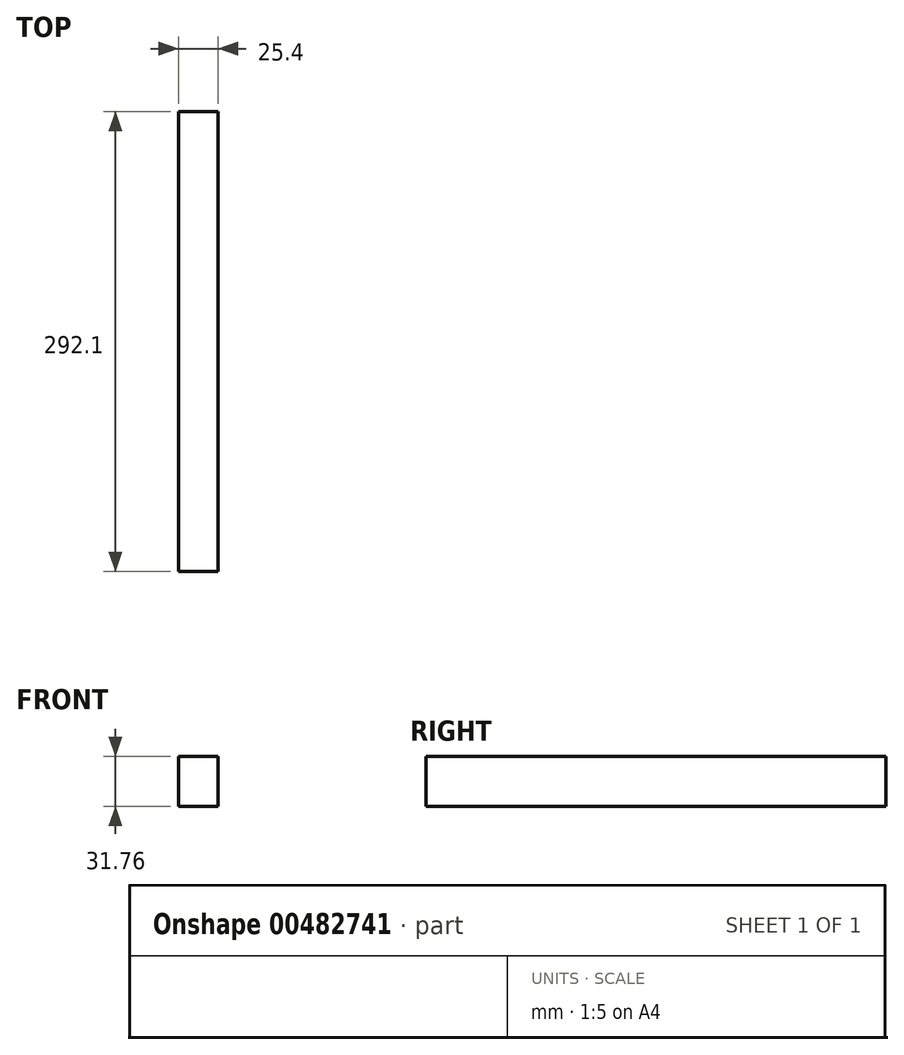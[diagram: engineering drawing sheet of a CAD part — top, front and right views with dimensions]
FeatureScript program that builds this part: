
annotation { "Feature Type Name" : "Feature", "Feature Type Description" : "" }
export const myFeature = defineFeature(function(context is Context, id is Id, definition is map)
    precondition{}
    {
        {
            var Q0;
            Q0=qCreatedBy(makeId("Right.planeOp"),FACE);
            var sketch = newSketch(context, id + "F0", { "sketchPlane" : qUnion([Q0])});
            skLineSegment(sketch, "E0.bottom", {"start": v(146.05, 15.88) * mm, "end": v(-146.05, 15.88) * mm});
            skLineSegment(sketch, "E0.top", {"start": v(146.05, -15.88) * mm, "end": v(-146.05, -15.88) * mm});
            skLineSegment(sketch, "E0.left", {"start": v(146.05, 15.88) * mm, "end": v(146.05, -15.88) * mm});
            skLineSegment(sketch, "E0.right", {"start": v(-146.05, 15.88) * mm, "end": v(-146.05, -15.88) * mm});
            skPoint(sketch, "E0.middle", {"position": v(0, 0) * mm});
            skSolve(sketch);
        }
        {
            var Q0;
            Q0=makeQuery(id+"F0.imprint","IMPRINT",FACE,{"disambiguationData":[TD([[makeQuery(id+"F0.imprint","IMPRINT",EDGE,{"derivedFrom":sQuery(id+"F0.wireOp",EDGE,"E0.bottom")}),1.0]])]});
            extrude(context, id + "F1", {"entities" : qUnion([Q0]), "depth" : 20.32 * mm});
        }
        {
            var Q0;
            Q0=makeQuery(id+"F1.opExtrude","CAP_FACE",FACE,{"disambiguationData":[OSD([sQuery(id+"F0.wireOp",EDGE,"E0.bottom"),sQuery(id+"F0.wireOp",EDGE,"E0.top"),sQuery(id+"F0.wireOp",EDGE,"E0.left"),sQuery(id+"F0.wireOp",EDGE,"E0.right")])],"isStart":false});
            extrude(context, id + "F2", {"entities" : qUnion([Q0]), "operationType" : NewBodyOperationType.ADD, "depth" : 5.08 * mm});
        }
        {
            var Q0;
            Q0=makeQuery(id+"F2.opExtrude","CAP_FACE",FACE,{"disambiguationData":[OSD([sQuery(id+"F0.wireOp",EDGE,"E0.bottom"),sQuery(id+"F0.wireOp",EDGE,"E0.top"),sQuery(id+"F0.wireOp",EDGE,"E0.left"),sQuery(id+"F0.wireOp",EDGE,"E0.right")])],"isStart":false});
            extrude(context, id + "F3", {"entities" : qUnion([Q0]), "operationType" : NewBodyOperationType.ADD, "depth" : 25.4 * mm});
        }
        {
            var Q0;
            Q0=makeQuery(id+"F3.opExtrude","CAP_FACE",FACE,{"disambiguationData":[OSD([sQuery(id+"F0.wireOp",EDGE,"E0.bottom"),sQuery(id+"F0.wireOp",EDGE,"E0.top"),sQuery(id+"F0.wireOp",EDGE,"E0.left"),sQuery(id+"F0.wireOp",EDGE,"E0.right")])],"isStart":false});
            extrude(context, id + "F4", {"entities" : qUnion([Q0]), "operationType" : NewBodyOperationType.REMOVE, "oppositeDirection" : true, "depth" : 25.4 * mm});
        }
    });
